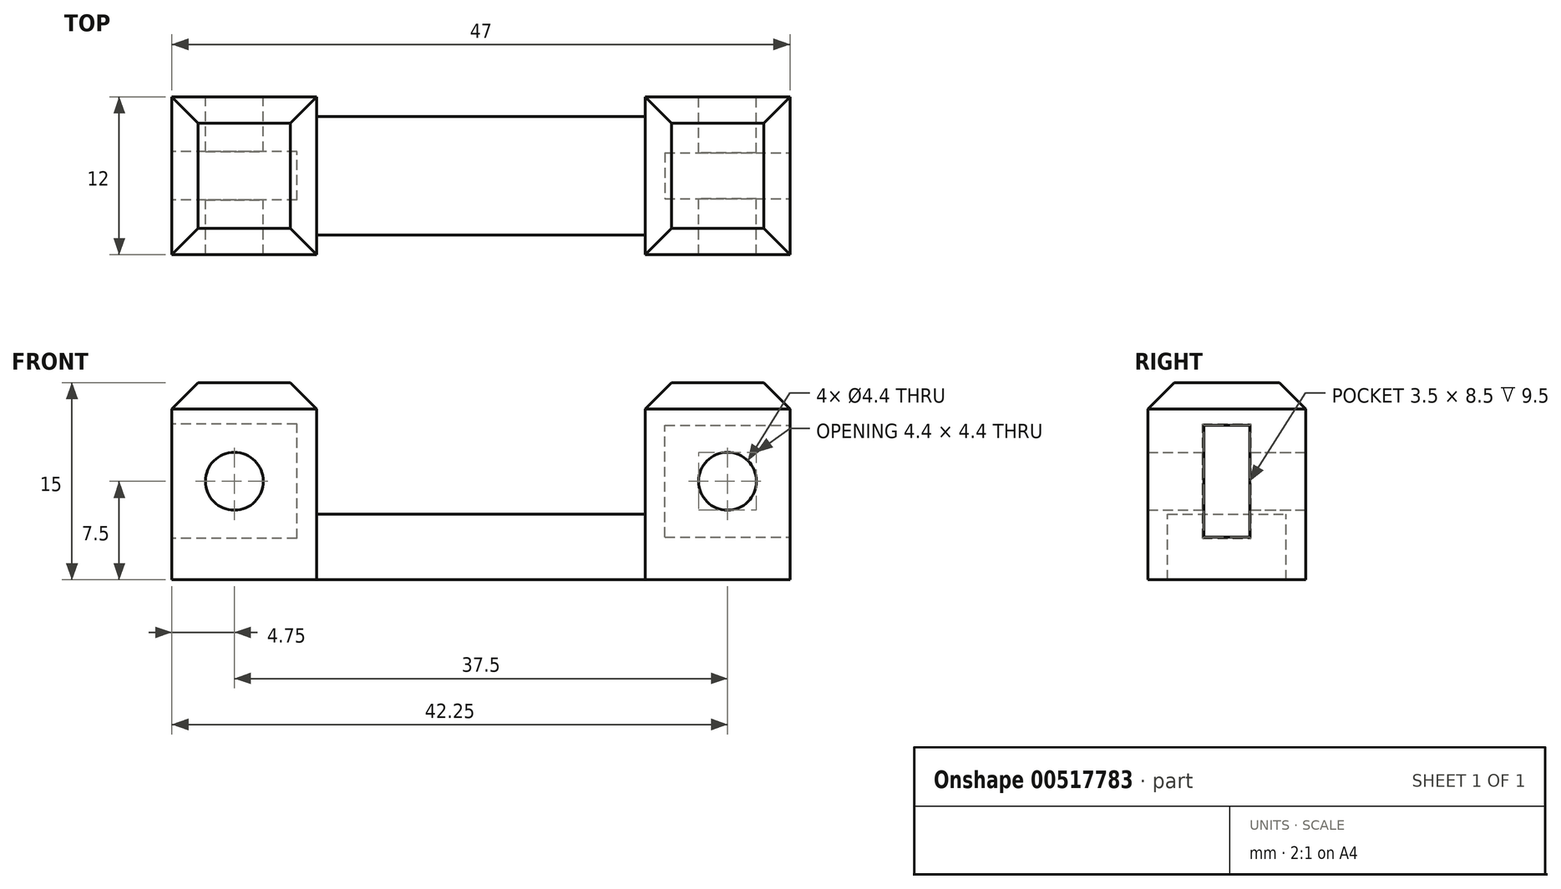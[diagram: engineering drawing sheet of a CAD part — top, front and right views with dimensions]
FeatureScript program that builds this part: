
annotation { "Feature Type Name" : "Feature", "Feature Type Description" : "" }
export const myFeature = defineFeature(function(context is Context, id is Id, definition is map)
    precondition{}
    {
        {
            var Q0;
            Q0=qCreatedBy(makeId("Front.planeOp"),FACE);
            var sketch = newSketch(context, id + "F0", { "sketchPlane" : qUnion([Q0])});
            skLineSegment(sketch, "E0.top", {"start": v(0, 15) * mm, "end": v(11, 15) * mm});
            skLineSegment(sketch, "E0.left", {"start": v(0, 0) * mm, "end": v(0, 15) * mm});
            skLineSegment(sketch, "E0.right", {"start": v(11, 5) * mm, "end": v(11, 15) * mm});
            skLineSegment(sketch, "E1.bottom", {"start": v(0, 0) * mm, "end": v(47, 0) * mm});
            skLineSegment(sketch, "E1.top", {"start": v(11, 5) * mm, "end": v(36, 5) * mm});
            skPoint(sketch, "E2", {"position": v(36, 5) * mm});
            skLineSegment(sketch, "E3", {"start": v(47, 0) * mm, "end": v(47, 15) * mm});
            skLineSegment(sketch, "E4", {"start": v(47, 15) * mm, "end": v(36, 15) * mm});
            skLineSegment(sketch, "E5", {"start": v(36, 15) * mm, "end": v(36, 5) * mm});
            skCircle(sketch, "E6", {"center": v(4.75, 7.5) * mm, "radius": 2.2 * mm});
            skCircle(sketch, "E7", {"center": v(42.25, 7.5) * mm, "radius": 2.2 * mm});
            skPoint(sketch, "E8", {"position": v(0, 7.5) * mm});
            skPoint(sketch, "E9", {"position": v(47, 7.5) * mm});
            skSolve(sketch);
        }
        {
            var Q0;
            Q0=makeQuery(id+"F0.imprint","IMPRINT",FACE,{"disambiguationData":[TD([[makeQuery(id+"F0.imprint","IMPRINT",EDGE,{"derivedFrom":sQuery(id+"F0.wireOp",EDGE,"E0.top")}),-1.0]])]});
            extrude(context, id + "F1", {"entities" : qUnion([Q0]), "depth" : 12 * mm, "offsetDistance" : 25 * mm});
        }
        {
            var Q0;
            Q0=makeQuery(id+"F1.opExtrude","SWEPT_FACE",FACE,{"disambiguationData":[OSD([sQuery(id+"F0.wireOp",EDGE,"E3")])]});
            var sketch = newSketch(context, id + "F2", { "sketchPlane" : qUnion([Q0])});
            skLineSegment(sketch, "E10.bottom", {"start": v(-4.25, 3.25) * mm, "end": v(-7.75, 3.25) * mm});
            skLineSegment(sketch, "E10.top", {"start": v(-4.25, 11.75) * mm, "end": v(-7.75, 11.75) * mm});
            skLineSegment(sketch, "E10.left", {"start": v(-4.25, 3.25) * mm, "end": v(-4.25, 11.75) * mm});
            skLineSegment(sketch, "E10.right", {"start": v(-7.75, 3.25) * mm, "end": v(-7.75, 11.75) * mm});
            skPoint(sketch, "E10.middle", {"position": v(-6, 7.5) * mm});
            skPoint(sketch, "E10.middle.positionSnap0", {"position": v(-6, 15) * mm});
            skPoint(sketch, "E10.middle.positionSnap1", {"position": v(-12, 7.5) * mm});
            skPoint(sketch, "E10.centerSnap0", {"position": v(-6, 15) * mm});
            skPoint(sketch, "E10.centerSnap1", {"position": v(-12, 7.5) * mm});
            skSolve(sketch);
        }
        {
            var Q0;
            Q0=makeQuery(id+"F2.imprint","IMPRINT",FACE,{"disambiguationData":[TD([[makeQuery(id+"F2.imprint","IMPRINT",EDGE,{"derivedFrom":sQuery(id+"F2.wireOp",EDGE,"E10.bottom")}),-1.0]])]});
            extrude(context, id + "F3", {"entities" : qUnion([Q0]), "operationType" : NewBodyOperationType.REMOVE, "oppositeDirection" : true, "depth" : 9.5 * mm, "offsetDistance" : 25 * mm});
        }
        {
            var Q0;
            Q0=makeQuery(id+"F1.opExtrude","SWEPT_FACE",FACE,{"disambiguationData":[OSD([sQuery(id+"F0.wireOp",EDGE,"E0.left")])]});
            var sketch = newSketch(context, id + "F4", { "sketchPlane" : qUnion([Q0])});
            skLineSegment(sketch, "E11.bottom", {"start": v(7.85, 3.15) * mm, "end": v(4.15, 3.15) * mm});
            skLineSegment(sketch, "E11.top", {"start": v(7.85, 11.85) * mm, "end": v(4.15, 11.85) * mm});
            skLineSegment(sketch, "E11.left", {"start": v(7.85, 3.15) * mm, "end": v(7.85, 11.85) * mm});
            skLineSegment(sketch, "E11.right", {"start": v(4.15, 3.15) * mm, "end": v(4.15, 11.85) * mm});
            skPoint(sketch, "E11.middle", {"position": v(6, 7.5) * mm});
            skPoint(sketch, "E11.middle.positionSnap0", {"position": v(6, 15) * mm});
            skPoint(sketch, "E11.middle.positionSnap1", {"position": v(0, 7.5) * mm});
            skPoint(sketch, "E11.centerSnap0", {"position": v(6, 15) * mm});
            skPoint(sketch, "E11.centerSnap1", {"position": v(0, 7.5) * mm});
            skSolve(sketch);
        }
        {
            var Q0;
            Q0 = qSketchRegion(id + "F4", true);
            extrude(context, id + "F5", {"entities" : qUnion([Q0]), "operationType" : NewBodyOperationType.REMOVE, "oppositeDirection" : true, "depth" : 9.5 * mm, "offsetDistance" : 25 * mm});
        }
        {
            var Q0;
            Q0=makeQuery(id+"F1.opExtrude","SWEPT_FACE",FACE,{"disambiguationData":[OSD([sQuery(id+"F0.wireOp",EDGE,"E1.top")])]});
            var sketch = newSketch(context, id + "F6", { "sketchPlane" : qUnion([Q0])});
            skLineSegment(sketch, "E12.bottom", {"start": v(11, 0) * mm, "end": v(36, 0) * mm});
            skLineSegment(sketch, "E12.top", {"start": v(11, -1.5) * mm, "end": v(36, -1.5) * mm});
            skLineSegment(sketch, "E12.left", {"start": v(11, 0) * mm, "end": v(11, -1.5) * mm});
            skLineSegment(sketch, "E12.right", {"start": v(36, 0) * mm, "end": v(36, -1.5) * mm});
            skLineSegment(sketch, "E13.bottom", {"start": v(11, -12) * mm, "end": v(36, -12) * mm});
            skLineSegment(sketch, "E13.top", {"start": v(11, -10.5) * mm, "end": v(36, -10.5) * mm});
            skLineSegment(sketch, "E13.left", {"start": v(11, -12) * mm, "end": v(11, -10.5) * mm});
            skLineSegment(sketch, "E13.right", {"start": v(36, -12) * mm, "end": v(36, -10.5) * mm});
            skSolve(sketch);
        }
        {
            var Q0;
            Q0 = qSketchRegion(id + "F6", true);
            extrude(context, id + "F7", {"entities" : qUnion([Q0]), "operationType" : NewBodyOperationType.REMOVE, "endBound" : BoundingType.THROUGH_ALL, "oppositeDirection" : true, "depth" : 25 * mm, "offsetDistance" : 25 * mm});
        }
        {
            var Q0;
            Q0=makeQuery(id+"F1.opExtrude","SWEPT_FACE",FACE,{"disambiguationData":[OSD([sQuery(id+"F0.wireOp",EDGE,"E0.top")])]});
            var Q1;
            Q1=makeQuery(id+"F1.opExtrude","SWEPT_FACE",FACE,{"disambiguationData":[OSD([sQuery(id+"F0.wireOp",EDGE,"E4")])]});
            chamfer(context, id + "F8", {"entities" : qUnion([Q0, Q1]), "width" : 2 * mm, "tangentPropagation" : true});
        }
    });
